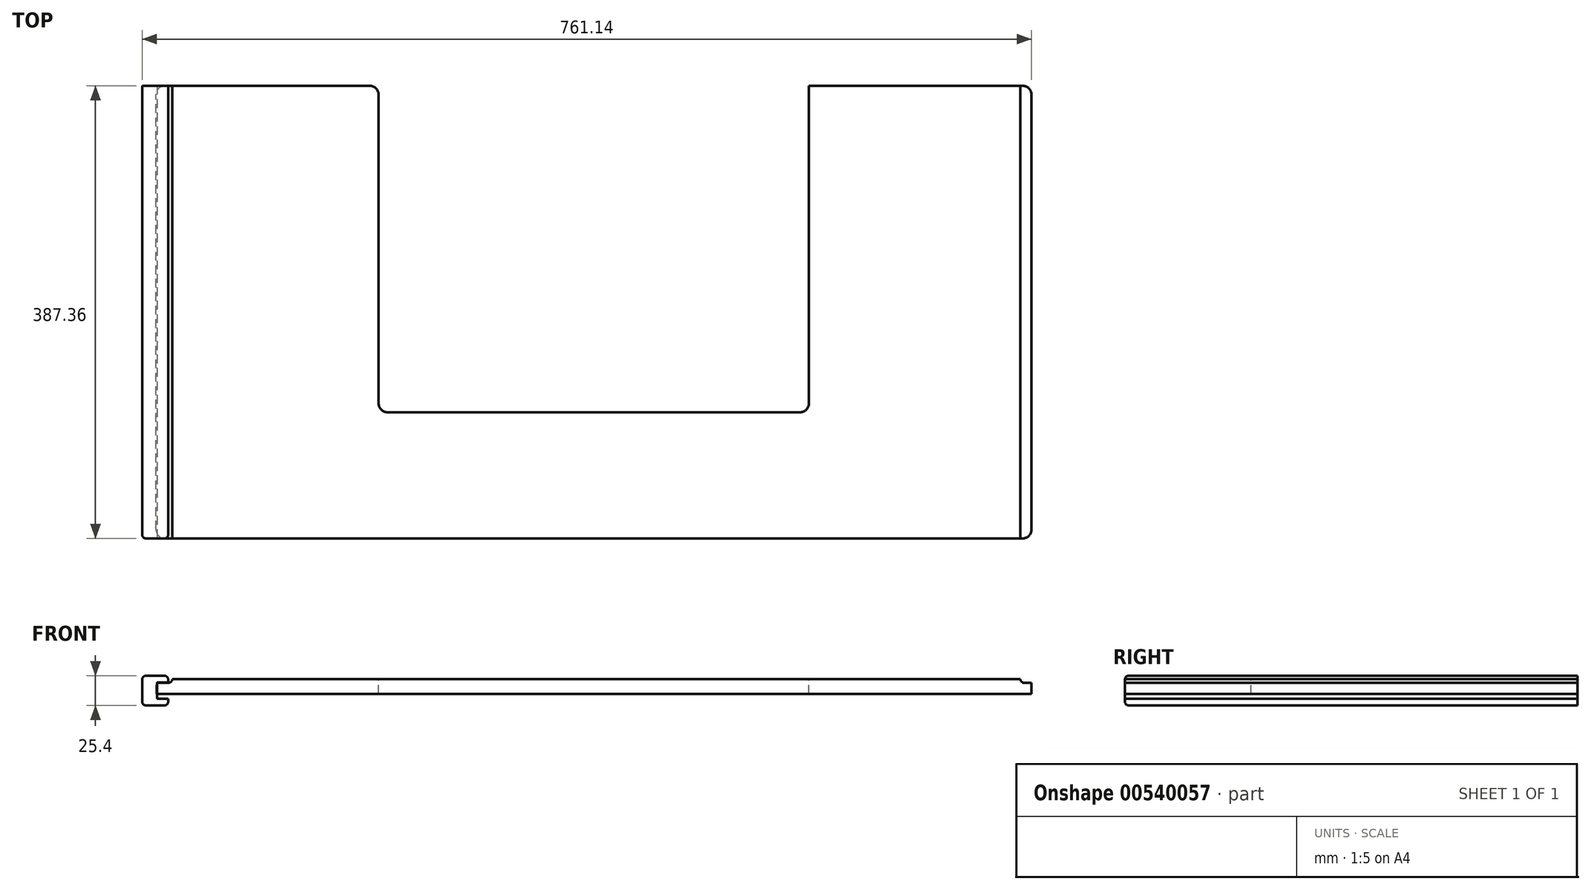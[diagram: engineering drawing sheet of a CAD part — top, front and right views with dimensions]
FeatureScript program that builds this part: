
annotation { "Feature Type Name" : "Feature", "Feature Type Description" : "" }
export const myFeature = defineFeature(function(context is Context, id is Id, definition is map)
    precondition{}
    {
        {
            var Q0;
            Q0=qCreatedBy(makeId("Front.planeOp"),FACE);
            var sketch = newSketch(context, id + "F0", { "sketchPlane" : qUnion([Q0])});
            skLineSegment(sketch, "E0.bottom", {"start": v(374.65, -6.35) * mm, "end": v(-374.65, -6.35) * mm});
            skLineSegment(sketch, "E0.top", {"start": v(374.65, 6.35) * mm, "end": v(-374.65, 6.35) * mm});
            skLineSegment(sketch, "E0.left", {"start": v(374.65, -6.35) * mm, "end": v(374.65, 6.35) * mm});
            skLineSegment(sketch, "E0.right", {"start": v(-374.65, -6.35) * mm, "end": v(-374.65, 6.35) * mm});
            skPoint(sketch, "E0.middle", {"position": v(0, 0) * mm});
            skSolve(sketch);
        }
        {
            var Q0;
            Q0 = qSketchRegion(id + "F0", true);
            extrude(context, id + "F1", {"entities" : qUnion([Q0]), "endBound" : BoundingType.SYMMETRIC, "depth" : 387.35 * mm, "offsetDistance" : 25.4 * mm});
        }
        {
            var Q0;
            Q0=makeQuery(id+"F1.opExtrude","SWEPT_FACE",FACE,{"disambiguationData":[OSD([sQuery(id+"F0.wireOp",EDGE,"E0.top")])]});
            var sketch = newSketch(context, id + "F2", { "sketchPlane" : qUnion([Q0])});
            skLineSegment(sketch, "E1.bottom", {"start": v(184.15, 193.68) * mm, "end": v(-184.15, 193.68) * mm});
            skLineSegment(sketch, "E1.top", {"start": v(184.15, -85.72) * mm, "end": v(-184.15, -85.73) * mm});
            skLineSegment(sketch, "E1.left", {"start": v(184.15, 193.68) * mm, "end": v(184.15, -85.72) * mm});
            skLineSegment(sketch, "E1.right", {"start": v(-184.15, 193.67) * mm, "end": v(-184.15, -85.72) * mm});
            skSolve(sketch);
        }
        {
            var Q0;
            Q0 = qSketchRegion(id + "F2", true);
            extrude(context, id + "F3", {"entities" : qUnion([Q0]), "operationType" : NewBodyOperationType.REMOVE, "endBound" : BoundingType.SYMMETRIC, "oppositeDirection" : true, "depth" : 25.4 * mm, "offsetDistance" : 25.4 * mm});
        }
        {
            var Q0;
            Q0=makeQuery(id+"F3.boolean.opBoolean","COPY",EDGE,{"derivedFrom":makeQuery(id+"F3.opExtrude","SWEPT_EDGE",EDGE,{"disambiguationData":[OSD([sQuery(id+"F0.wireOp",EDGE,"E0.top"),sQuery(id+"F2.wireOp",EDGE,"E1.bottom"),sQuery(id+"F2.wireOp",EDGE,"E1.right")])]})});
            var Q1;
            Q1=makeQuery(id+"F1.opExtrude","CAP_EDGE",EDGE,{"disambiguationData":[OSD([sQuery(id+"F0.wireOp",EDGE,"E0.right")])],"isStart":true});
            var Q2;
            Q2=makeQuery(id+"F3.boolean.opBoolean","COPY",EDGE,{"derivedFrom":makeQuery(id+"F3.opExtrude","SWEPT_EDGE",EDGE,{"disambiguationData":[OSD([sQuery(id+"F2.wireOp",EDGE,"E1.top"),sQuery(id+"F2.wireOp",EDGE,"E1.right")])]})});
            var Q3;
            Q3=makeQuery(id+"F3.boolean.opBoolean","COPY",EDGE,{"derivedFrom":makeQuery(id+"F3.opExtrude","SWEPT_EDGE",EDGE,{"disambiguationData":[OSD([sQuery(id+"F2.wireOp",EDGE,"E1.top"),sQuery(id+"F2.wireOp",EDGE,"E1.left")])]})});
            var Q4;
            Q4=makeQuery(id+"F3.boolean.opBoolean","COPY",EDGE,{"derivedFrom":makeQuery(id+"F3.opExtrude","SWEPT_EDGE",EDGE,{"disambiguationData":[OSD([sQuery(id+"F0.wireOp",EDGE,"E0.top"),sQuery(id+"F2.wireOp",EDGE,"E1.bottom"),sQuery(id+"F2.wireOp",EDGE,"E1.left")])]})});
            var Q5;
            Q5=makeQuery(id+"F1.opExtrude","CAP_EDGE",EDGE,{"disambiguationData":[OSD([sQuery(id+"F0.wireOp",EDGE,"E0.left")])],"isStart":true});
            var Q6;
            Q6=makeQuery(id+"F1.opExtrude","CAP_EDGE",EDGE,{"disambiguationData":[OSD([sQuery(id+"F0.wireOp",EDGE,"E0.left")])],"isStart":false});
            var Q7;
            Q7=makeQuery(id+"F1.opExtrude","CAP_EDGE",EDGE,{"disambiguationData":[OSD([sQuery(id+"F0.wireOp",EDGE,"E0.right")])],"isStart":false});
            fillet(context, id + "F4", {"entities" : qUnion([Q0, Q1, Q2, Q3, Q4, Q5, Q6, Q7]), "radius" : 7.62 * mm, "tangentPropagation" : true, "allowEdgeOverflow" : false});
        }
        {
            var Q0;
            Q0=makeQuery(id+"F2.imprint","IMPRINT",FACE,{"disambiguationData":[TD([[makeQuery(id+"F2.imprint","IMPRINT",EDGE,{"derivedFrom":sQuery(id+"F2.wireOp",EDGE,"E1.top")}),1.0]])]});
            var sketch = newSketch(context, id + "F5", { "sketchPlane" : qUnion([Q0])});
            skLineSegment(sketch, "E2.bottom", {"start": v(-360.7, 193.68) * mm, "end": v(-368.3, 193.68) * mm});
            skLineSegment(sketch, "E2.top", {"start": v(-360.7, -193.68) * mm, "end": v(-374.65, -193.68) * mm});
            skLineSegment(sketch, "E2.left", {"start": v(-360.7, 193.68) * mm, "end": v(-360.7, -193.68) * mm});
            skLineSegment(sketch, "E2.right", {"start": v(-374.65, 187.33) * mm, "end": v(-374.65, -193.68) * mm});
            skPoint(sketch, "E3.visualSharp", {"position": v(-374.65, 193.68) * mm});
            skArc(sketch, "E3.filletArc", {"start": v(-368.3, 193.68) * mm, "mid": v(-372.8, 191.82) * mm, "end": v(-374.65, 187.33) * mm});
            skSolve(sketch);
        }
        {
            var Q0;
            {var subQ10=sQuery(id+"F5.wireOp",EDGE,"E2.bottom");Q0=makeQuery(id+"F5.imprint","IMPRINT",FACE,{"disambiguationData":[TD([[makeQuery(id+"F5.imprint","IMPRINT",EDGE,{"derivedFrom":subQ10}),1.0]])]});}
            var Q1;
            Q1 = qConstructionFilter(qBodyType(qCreatedBy(id + "F5" ,EDGE), BodyType.WIRE), ConstructionObject.NO);
            extrude(context, id + "F6", {"entities" : qUnion([Q0]), "operationType" : NewBodyOperationType.REMOVE, "surfaceEntities" : qUnion([Q1]), "oppositeDirection" : true, "depth" : 3.17 * mm, "offsetDistance" : 25.4 * mm});
        }
        {
            var Q0;
            Q0=makeQuery(id+"F1.opExtrude","CAP_FACE",FACE,{"disambiguationData":[OSD([sQuery(id+"F0.wireOp",EDGE,"E0.bottom"),sQuery(id+"F0.wireOp",EDGE,"E0.top"),sQuery(id+"F0.wireOp",EDGE,"E0.left"),sQuery(id+"F0.wireOp",EDGE,"E0.right")])],"isStart":false});
            var sketch = newSketch(context, id + "F7", { "sketchPlane" : qUnion([Q0])});
            skLineSegment(sketch, "E4", {"start": v(-360.7, 6.35) * mm, "end": v(-360.7, 6.35) * mm});
            skLineSegment(sketch, "E5", {"start": v(-363.88, 3.17) * mm, "end": v(-363.88, 3.17) * mm});
            skPoint(sketch, "E6.visualSharp", {"position": v(-360.7, 3.17) * mm});
            skArc(sketch, "E6.filletArc", {"start": v(-363.88, 3.17) * mm, "mid": v(-361.64, 4.1) * mm, "end": v(-360.7, 6.35) * mm});
            skLineSegment(sketch, "E7", {"start": v(-363.88, 3.17) * mm, "end": v(-360.7, 3.17) * mm});
            skLineSegment(sketch, "E8", {"start": v(-360.7, 6.35) * mm, "end": v(-360.7, 3.17) * mm});
            skSolve(sketch);
        }
        {
            var Q0;
            Q0 = qSketchRegion(id + "F7", true);
            extrude(context, id + "F8", {"entities" : qUnion([Q0]), "operationType" : NewBodyOperationType.ADD, "oppositeDirection" : true, "depth" : 387.35 * mm, "offsetDistance" : 25.4 * mm});
        }
        {
            var Q0;
            Q0=makeQuery(id+"F2.imprint","IMPRINT",FACE,{"disambiguationData":[TD([[makeQuery(id+"F2.imprint","IMPRINT",EDGE,{"derivedFrom":sQuery(id+"F2.wireOp",EDGE,"E1.top")}),1.0]])]});
            var sketch = newSketch(context, id + "F9", { "sketchPlane" : qUnion([Q0])});
            skLineSegment(sketch, "E9.bottom", {"start": v(365.13, 193.68) * mm, "end": v(374.65, 193.68) * mm});
            skLineSegment(sketch, "E9.top", {"start": v(365.13, -193.68) * mm, "end": v(374.65, -193.68) * mm});
            skLineSegment(sketch, "E9.left", {"start": v(365.12, 193.68) * mm, "end": v(365.12, -193.68) * mm});
            skLineSegment(sketch, "E9.right", {"start": v(374.65, 193.68) * mm, "end": v(374.65, -193.68) * mm});
            skSolve(sketch);
        }
        {
            var Q0;
            Q0 = qSketchRegion(id + "F9", true);
            extrude(context, id + "F10", {"entities" : qUnion([Q0]), "operationType" : NewBodyOperationType.REMOVE, "oppositeDirection" : true, "depth" : 3.17 * mm, "offsetDistance" : 25.4 * mm});
        }
        {
            var Q0;
            Q0=makeQuery(id+"F8.boolean.opBoolean","MERGE",FACE,{"derivedFrom":[makeQuery(id+"F1.opExtrude","CAP_FACE",FACE,{"disambiguationData":[OSD([sQuery(id+"F0.wireOp",EDGE,"E0.bottom"),sQuery(id+"F0.wireOp",EDGE,"E0.top"),sQuery(id+"F0.wireOp",EDGE,"E0.left"),sQuery(id+"F0.wireOp",EDGE,"E0.right")])],"isStart":false}),makeQuery(id+"F8.opExtrude","CAP_FACE",FACE,{"disambiguationData":[OSD([sQuery(id+"F7.wireOp",EDGE,"E6.filletArc"),sQuery(id+"F7.wireOp",EDGE,"E7"),sQuery(id+"F7.wireOp",EDGE,"E8")])],"isStart":true})]});
            var sketch = newSketch(context, id + "F11", { "sketchPlane" : qUnion([Q0])});
            skLineSegment(sketch, "E10", {"start": v(365.13, 6.35) * mm, "end": v(365.13, 6.35) * mm});
            skLineSegment(sketch, "E11", {"start": v(368.3, 3.18) * mm, "end": v(368.3, 3.18) * mm});
            skPoint(sketch, "E12.visualSharp", {"position": v(365.13, 3.18) * mm});
            skArc(sketch, "E12.filletArc", {"start": v(365.13, 6.35) * mm, "mid": v(366.05, 4.1) * mm, "end": v(368.3, 3.18) * mm});
            skLineSegment(sketch, "E13", {"start": v(365.13, 6.35) * mm, "end": v(365.13, 3.18) * mm});
            skLineSegment(sketch, "E14", {"start": v(365.13, 3.18) * mm, "end": v(368.3, 3.18) * mm});
            skSolve(sketch);
        }
        {
            var Q0;
            Q0 = qSketchRegion(id + "F11", true);
            extrude(context, id + "F12", {"entities" : qUnion([Q0]), "operationType" : NewBodyOperationType.ADD, "oppositeDirection" : true, "depth" : 387.35 * mm, "offsetDistance" : 25.4 * mm});
        }
        {
            var Q0;
            Q0=makeQuery(id+"F12.boolean.opBoolean","MERGE",FACE,{"derivedFrom":[makeQuery(id+"F8.boolean.opBoolean","MERGE",FACE,{"derivedFrom":[makeQuery(id+"F1.opExtrude","CAP_FACE",FACE,{"disambiguationData":[OSD([sQuery(id+"F0.wireOp",EDGE,"E0.bottom"),sQuery(id+"F0.wireOp",EDGE,"E0.top"),sQuery(id+"F0.wireOp",EDGE,"E0.left"),sQuery(id+"F0.wireOp",EDGE,"E0.right")])],"isStart":false}),makeQuery(id+"F8.opExtrude","CAP_FACE",FACE,{"disambiguationData":[OSD([sQuery(id+"F7.wireOp",EDGE,"E6.filletArc"),sQuery(id+"F7.wireOp",EDGE,"E7"),sQuery(id+"F7.wireOp",EDGE,"E8")])],"isStart":true})]}),makeQuery(id+"F12.opExtrude","CAP_FACE",FACE,{"disambiguationData":[OSD([sQuery(id+"F11.wireOp",EDGE,"E12.filletArc"),sQuery(id+"F11.wireOp",EDGE,"E13"),sQuery(id+"F11.wireOp",EDGE,"E14")])],"isStart":true})]});
            var sketch = newSketch(context, id + "F13", { "sketchPlane" : qUnion([Q0])});
            skLineSegment(sketch, "E15.bottom", {"start": v(-364.26, 9.14) * mm, "end": v(-386.49, 9.14) * mm});
            skLineSegment(sketch, "E15.top", {"start": v(-364.26, -16.26) * mm, "end": v(-386.49, -16.26) * mm});
            skLineSegment(sketch, "E15.right", {"start": v(-386.49, 9.14) * mm, "end": v(-386.49, -16.26) * mm});
            skPoint(sketch, "E16.visualSharp", {"position": v(-361.09, 3.56) * mm});
            skPoint(sketch, "E17.visualSharp", {"position": v(-361.09, -6.73) * mm});
            skPoint(sketch, "E18.visualSharp", {"position": v(-361.09, 9.14) * mm});
            skPoint(sketch, "E19.visualSharp", {"position": v(-378.9, 9.14) * mm});
            skPoint(sketch, "E20.visualSharp", {"position": v(-386.49, -16.26) * mm});
            skPoint(sketch, "E21.visualSharp", {"position": v(-361.09, -16.26) * mm});
            skLineSegment(sketch, "E22", {"start": v(-364.26, 3.56) * mm, "end": v(-373.79, 3.56) * mm});
            skLineSegment(sketch, "E23", {"start": v(-373.79, -10.67) * mm, "end": v(-364.26, -10.67) * mm});
            skLineSegment(sketch, "E24", {"start": v(-364.26, 9.14) * mm, "end": v(-364.26, 3.56) * mm});
            skLineSegment(sketch, "E25.trimOffspring", {"start": v(-364.26, -10.67) * mm, "end": v(-364.26, -16.26) * mm});
            skPoint(sketch, "E26.end.orphan", {"position": v(-373.79, 0) * mm});
            skPoint(sketch, "E27.start.orphan", {"position": v(-373.79, -3.56) * mm});
            skLineSegment(sketch, "E28", {"start": v(-373.79, 3.56) * mm, "end": v(-373.79, -10.67) * mm});
            skSolve(sketch);
        }
        {
            var Q0;
            Q0=makeQuery(id+"F13.imprint","IMPRINT",FACE,{"disambiguationData":[TD([[makeQuery(id+"F13.imprint","IMPRINT",EDGE,{"derivedFrom":sQuery(id+"F13.wireOp",EDGE,"E15.bottom")}),1.0]])]});
            extrude(context, id + "F14", {"entities" : qUnion([Q0]), "oppositeDirection" : true, "depth" : 387.35 * mm, "offsetDistance" : 25.4 * mm});
        }
        {
            var Q0;
            Q0=makeQuery(id+"F1.opExtrude","SWEPT_BODY",BODY,{"disambiguationData":[OSD([sQuery(id+"F0.wireOp",EDGE,"E0.bottom"),sQuery(id+"F0.wireOp",EDGE,"E0.top"),sQuery(id+"F0.wireOp",EDGE,"E0.left"),sQuery(id+"F0.wireOp",EDGE,"E0.right")])]});
            transform(context, id + "F15", {"entities" : qUnion([Q0]), "transformType" : TransformType.TRANSLATION_3D, "dx" : 0 * mm, "dy" : 0 * mm, "dz" : 0 * mm, "makeCopy" : true});
        }
        {
            var Q0;
            Q0=makeQuery(id+"F14.opExtrude","SWEPT_EDGE",EDGE,{"disambiguationData":[OSD([sQuery(id+"F13.wireOp",EDGE,"E15.bottom"),sQuery(id+"F13.wireOp",EDGE,"E15.right")])]});
            var Q1;
            Q1=makeQuery(id+"F14.opExtrude","CAP_EDGE",EDGE,{"disambiguationData":[OSD([sQuery(id+"F13.wireOp",EDGE,"E15.bottom")])],"isStart":true});
            var Q2;
            Q2=makeQuery(id+"F14.opExtrude","CAP_EDGE",EDGE,{"disambiguationData":[OSD([sQuery(id+"F13.wireOp",EDGE,"E15.right")])],"isStart":true});
            var Q3;
            Q3=makeQuery(id+"F14.opExtrude","SWEPT_EDGE",EDGE,{"disambiguationData":[OSD([sQuery(id+"F13.wireOp",EDGE,"E15.top"),sQuery(id+"F13.wireOp",EDGE,"E15.right")])]});
            var Q4;
            Q4=makeQuery(id+"F14.opExtrude","CAP_EDGE",EDGE,{"disambiguationData":[OSD([sQuery(id+"F13.wireOp",EDGE,"E15.top")])],"isStart":true});
            var Q5;
            Q5=makeQuery(id+"F14.opExtrude","CAP_EDGE",EDGE,{"disambiguationData":[OSD([sQuery(id+"F13.wireOp",EDGE,"E25.trimOffspring")])],"isStart":true});
            var Q6;
            Q6=makeQuery(id+"F14.opExtrude","CAP_EDGE",EDGE,{"disambiguationData":[OSD([sQuery(id+"F13.wireOp",EDGE,"E24")])],"isStart":true});
            var Q7;
            Q7=makeQuery(id+"F14.opExtrude","SWEPT_EDGE",EDGE,{"disambiguationData":[OSD([sQuery(id+"F13.wireOp",EDGE,"E15.bottom"),sQuery(id+"F13.wireOp",EDGE,"E24")])]});
            var Q8;
            Q8=makeQuery(id+"F14.opExtrude","SWEPT_EDGE",EDGE,{"disambiguationData":[OSD([sQuery(id+"F13.wireOp",EDGE,"E15.top"),sQuery(id+"F13.wireOp",EDGE,"E25.trimOffspring")])]});
            fillet(context, id + "F16", {"entities" : qUnion([Q0, Q1, Q2, Q3, Q4, Q5, Q6, Q7, Q8]), "radius" : 3.17 * mm, "tangentPropagation" : true, "allowEdgeOverflow" : false});
        }
    });
